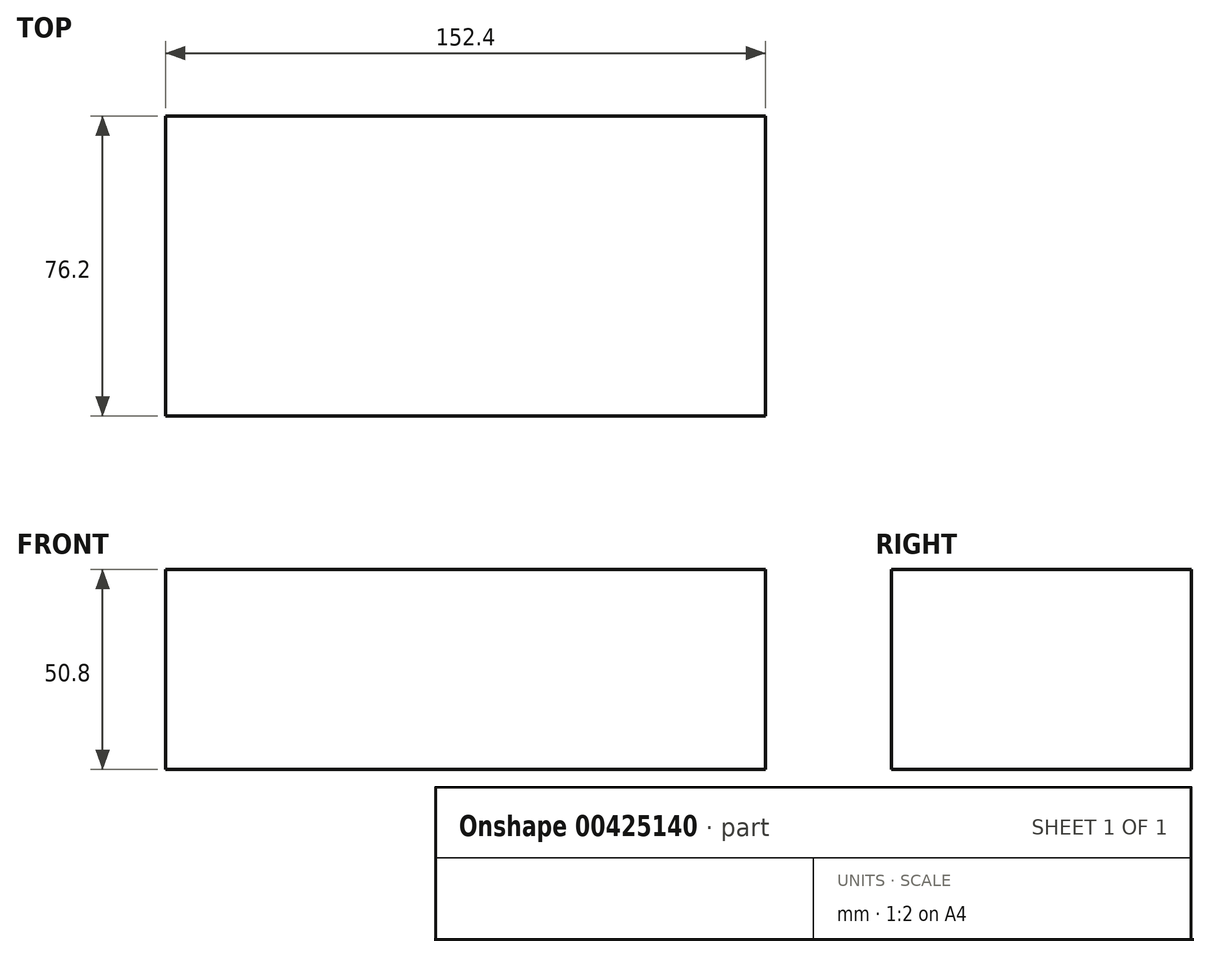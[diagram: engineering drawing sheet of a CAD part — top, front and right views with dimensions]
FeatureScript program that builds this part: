
annotation { "Feature Type Name" : "Feature", "Feature Type Description" : "" }
export const myFeature = defineFeature(function(context is Context, id is Id, definition is map)
    precondition{}
    {
        {
            var Q0;
            Q0=qCreatedBy(makeId("Front.planeOp"),FACE);
            var sketch = newSketch(context, id + "F0", { "sketchPlane" : qUnion([Q0])});
            skLineSegment(sketch, "E0", {"start": v(0, 0) * mm, "end": v(152.4, 0) * mm});
            skLineSegment(sketch, "E1", {"start": v(152.4, 0) * mm, "end": v(152.4, 50.8) * mm});
            skLineSegment(sketch, "E2", {"start": v(152.4, 50.8) * mm, "end": v(0, 50.8) * mm});
            skLineSegment(sketch, "E3", {"start": v(0, 50.8) * mm, "end": v(0, 0) * mm});
            skSolve(sketch);
        }
        {
            var Q0;
            Q0=makeQuery(id+"F0.imprint","IMPRINT",FACE,{"disambiguationData":[TD([[makeQuery(id+"F0.imprint","IMPRINT",EDGE,{"derivedFrom":sQuery(id+"F0.wireOp",EDGE,"E0")}),1.0]])]});
            extrude(context, id + "F1", {"entities" : qUnion([Q0]), "depth" : 76.2 * mm});
        }
    });
